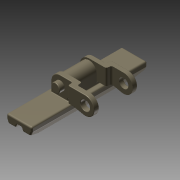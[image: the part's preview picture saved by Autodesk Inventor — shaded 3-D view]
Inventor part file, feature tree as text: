
AUTODESK INVENTOR PART (.ipt)
format: ipt  version: 2013 (Build 170138000, 138)  size: 1,072,640 bytes
history: native  units: mm (DEFAULTED — no unit token found)
features: plane x2, other x2, projected_geometry x2, imported_body x1, sketch x1
ambient origin geometry x8: Origin, YZ Plane, XZ Plane, XY Plane, X Axis, Y Axis, Z Axis, Center Point
bodies: Solid1 (feature_tree)
feature tree (8):
  imported_body  "Base1"
  plane  "Work Plane1"
  plane  "Work Plane2"
  other  "Work Axis2"
  sketch  "Sketch2"  dims[d2=90.0deg d4=5.0mm]
  other  "Work Axis1"
  projected_geometry  "Projected Loop2"
  projected_geometry  "Projected Loop3"
